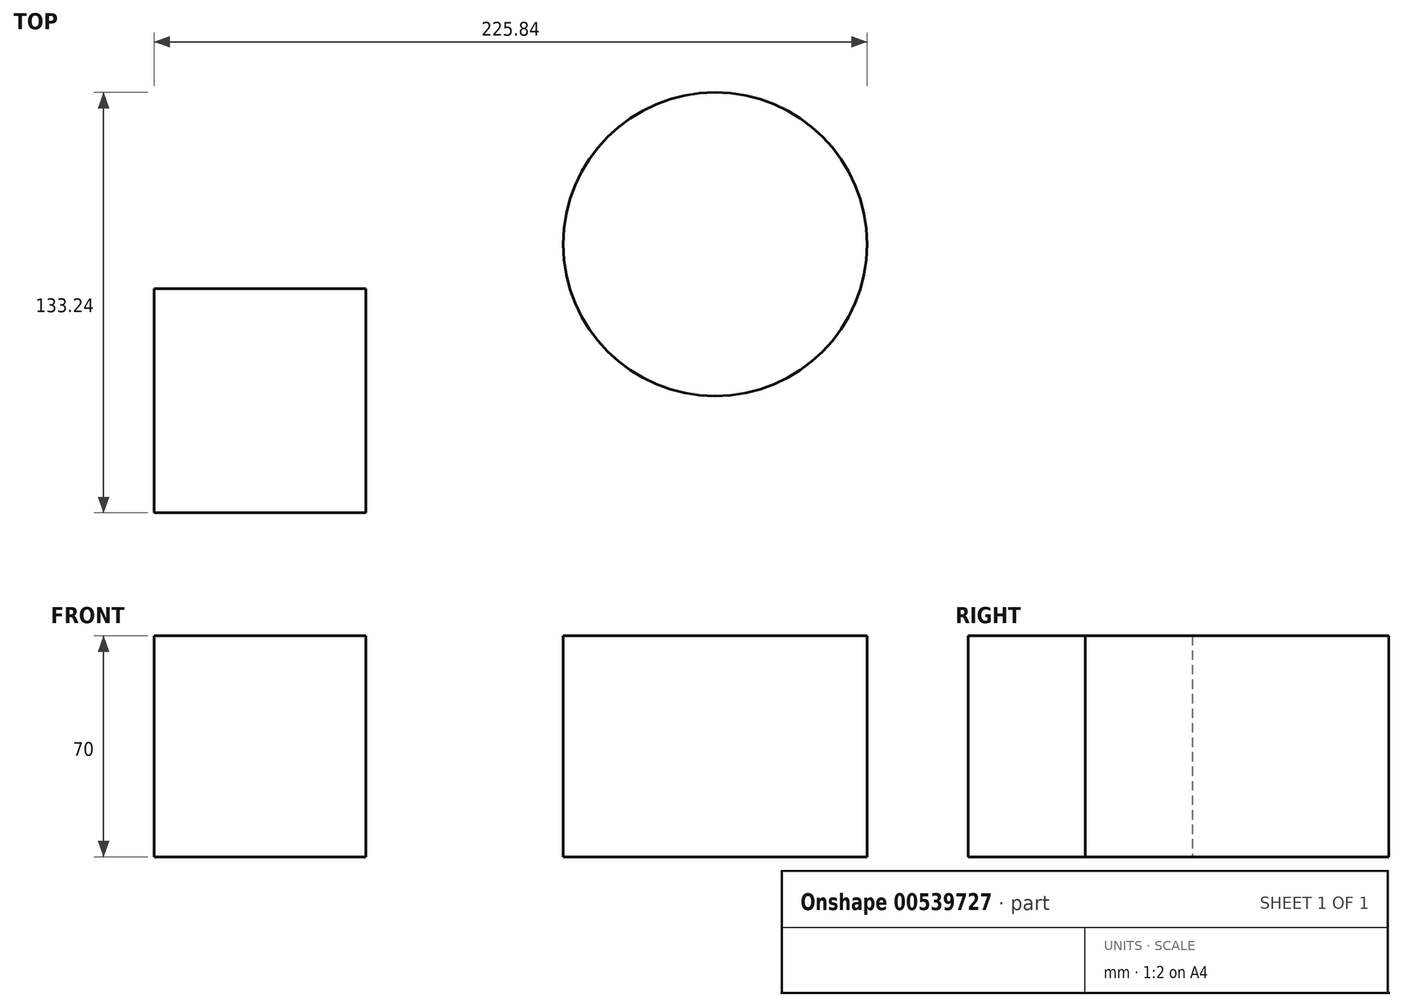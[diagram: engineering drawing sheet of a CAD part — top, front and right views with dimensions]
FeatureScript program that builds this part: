
annotation { "Feature Type Name" : "Feature", "Feature Type Description" : "" }
export const myFeature = defineFeature(function(context is Context, id is Id, definition is map)
    precondition{}
    {
        {
            var Q0;
            Q0=qCreatedBy(makeId("Top.planeOp"),FACE);
            var sketch = newSketch(context, id + "F0", { "sketchPlane" : qUnion([Q0])});
            skLineSegment(sketch, "E0.bottom", {"start": v(-118.05, -47.59) * mm, "end": v(-51, -47.59) * mm});
            skLineSegment(sketch, "E0.top", {"start": v(-118.05, 23.42) * mm, "end": v(-51, 23.42) * mm});
            skLineSegment(sketch, "E0.left", {"start": v(-118.05, -47.59) * mm, "end": v(-118.05, 23.42) * mm});
            skLineSegment(sketch, "E0.right", {"start": v(-51, -47.59) * mm, "end": v(-51, 23.42) * mm});
            skCircle(sketch, "E1", {"center": v(59.68, 37.55) * mm, "radius": 48.1 * mm});
            skSolve(sketch);
        }
        {
            var Q0;
            Q0=makeQuery(id+"F0.imprint","IMPRINT",FACE,{"disambiguationData":[TD([[makeQuery(id+"F0.imprint","IMPRINT",EDGE,{"derivedFrom":sQuery(id+"F0.wireOp",EDGE,"E0.bottom")}),1.0]])]});
            var Q1;
            Q1=makeQuery(id+"F0.imprint","IMPRINT",FACE,{"disambiguationData":[TD([[makeQuery(id+"F0.imprint","IMPRINT",EDGE,{"derivedFrom":sQuery(id+"F0.wireOp",EDGE,"E1")}),1.0]])]});
            extrude(context, id + "F1", {"entities" : qUnion([Q0, Q1]), "depth" : 70 * mm, "offsetDistance" : 25 * mm});
        }
    });
